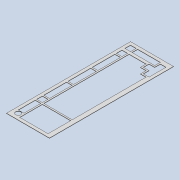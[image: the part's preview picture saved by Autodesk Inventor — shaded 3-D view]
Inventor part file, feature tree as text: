
AUTODESK INVENTOR PART (.ipt)
format: ipt  version: 2021 (Build 250183000, 183)  size: 449,024 bytes
history: native  units: mm
features: sketch x1, extrude x1
ambient origin geometry x8: Origin, YZ Plane, XZ Plane, XY Plane, X Axis, Y Axis, Z Axis, Center Point
bodies: Solid1 (feature_tree)
feature tree (2):
  sketch  "Sketch1"  dims[d0=37.05mm d1=18.0mm d2=0.0mm d3=0.0mm d4=18.0mm d5=1.05mm d6=37.05mm d7=18.0mm d8=1.05mm d10=18.0mm d12=18.0mm d13=18.0mm d15=18.0mm d16=18.0mm d17=1.05mm d18=1.05mm d21=18.0mm d25=1.05mm d26=37.05mm d27=18.0mm d33=1.05mm d34=18.0mm d37=22.7625mm d38=5.8125mm d39=22.7625mm d40=22.7625mm d41=1.05mm d42=1.05mm d43=1.05mm d44=1.05mm d45=1.05mm d46=1.05mm d47=18.0mm d48=18.0mm d49=18.0mm d50=118.0mm d51=41.8125mm d52=1.05mm d53=32.2875mm d54=27.525mm d55=18.0mm d56=1.05mm d57=1.05mm d58=1.05mm d59=1.05mm d60=1.05mm d61=1.05mm d62=1.05mm d63=1.05mm d64=1.05mm d66=18.0mm d67=18.0mm d68=18.0mm d69=18.0mm d70=18.0mm d71=18.0mm d72=18.0mm d73=18.0mm d74=18.0mm d75=18.0mm d76=1.05mm d77=1.05mm d78=32.2875mm d79=18.0mm d80=18.0mm d81=1.05mm d82=1.05mm d83=1.05mm d84=1.05mm d85=1.05mm d86=18.0mm d87=18.0mm d88=18.0mm d89=1.05mm d90=1.05mm d91=1.05mm d92=1.05mm d93=1.05mm d94=1.05mm d95=1.05mm d96=18.0mm d97=18.0mm d98=18.0mm d99=18.0mm d100=18.0mm d101=18.0mm d102=41.8125mm d103=1.05mm d104=1.05mm d105=1.05mm d106=1.05mm d107=1.05mm d108=1.05mm d109=1.05mm d110=1.05mm d111=1.05mm d112=1.05mm d116=18.0mm d117=18.0mm d118=18.0mm d119=18.0mm d120=18.0mm d121=18.0mm d122=18.0mm d123=18.0mm d124=18.0mm d125=18.0mm d127=18.0mm d128=18.0mm d129=1.05mm d130=1.05mm d131=27.525mm d132=1.05mm d133=18.0mm d134=18.0mm d135=18.0mm d136=1.05mm d137=1.05mm d138=1.05mm d139=1.05mm d140=1.05mm d141=1.05mm d142=1.05mm d143=1.05mm d144=1.05mm d145=1.05mm d146=1.05mm d147=1.05mm d148=1.05mm d149=37.05mm d150=18.0mm d151=18.0mm d152=18.0mm d153=18.0mm d154=18.0mm d155=18.0mm d156=18.0mm d157=18.0mm d158=18.0mm d159=1.05mm d160=1.05mm d161=1.05mm d162=1.05mm d163=1.05mm d164=1.05mm d165=5.8125mm d166=5.8125mm d168=5.8125mm d169=5.8125mm d170=18.0mm d171=18.0mm d172=18.0mm d173=1.05mm d174=1.05mm d176=1.05mm d178=1.05mm d179=1.05mm d180=1.05mm d181=1.05mm d182=1.05mm d183=18.0mm d184=18.0mm d185=18.0mm d186=18.0mm d187=18.0mm d188=18.0mm d189=18.0mm d191=18.0mm d192=18.0mm d193=18.0mm d194=5.8125mm d195=1.05mm d196=5.8125mm d197=18.0mm d198=18.0mm d199=18.0mm d200=18.0mm d201=18.0mm d202=18.0mm d203=18.0mm d204=1.05mm d205=1.05mm d206=1.05mm d207=18.0mm d208=18.0mm d209=18.0mm d210=18.0mm d211=1.05mm d212=18.0mm d213=18.0mm d214=1.05mm d215=1.05mm d216=18.0mm d218=5.8125mm d219=5.8125mm d220=5.8125mm d221=5.8125mm d223=17.0mm d224=17.5mm d225=0.5mm d226=0.5mm d227=0.5mm d228=0.5mm d229=0.5mm d230=0.5mm d231=0.5mm d232=0.5mm d233=0.5mm d234=0.5mm d235=0.5mm d236=0.5mm d237=0.5mm d238=0.5mm d239=0.5mm d240=0.5mm d241=0.5mm d242=0.5mm d243=0.5mm d244=0.5mm d245=0.5mm d246=0.5mm d247=0.5mm d248=0.5mm d249=0.5mm d250=0.5mm d251=0.5mm d253=0.5mm d254=0.5mm d255=0.5mm d256=0.5mm d257=0.5mm d258=0.5mm d259=0.5mm d260=0.5mm d261=0.5mm d262=0.5mm d263=0.5mm d264=10.05mm d265=14.8125mm d266=10.0mm d267=10.0mm d268=10.0mm d269=10.0mm d270=1.0mm d271=0.0mm]
  extrude  "Extrusion1"  Depth=1.0mm
